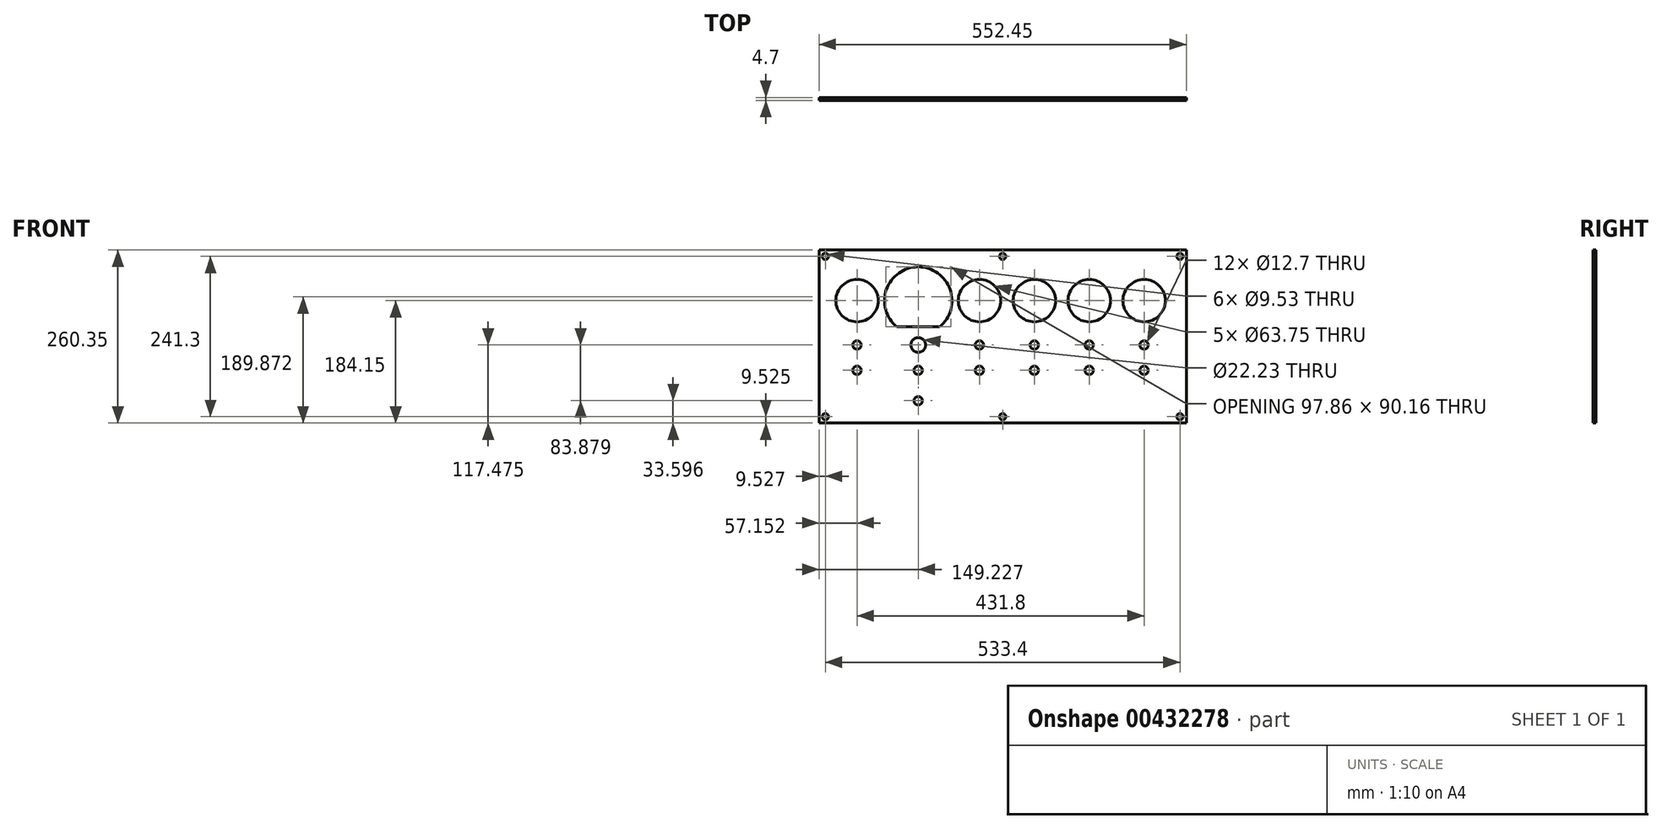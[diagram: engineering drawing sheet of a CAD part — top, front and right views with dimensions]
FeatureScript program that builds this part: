
annotation { "Feature Type Name" : "Feature", "Feature Type Description" : "" }
export const myFeature = defineFeature(function(context is Context, id is Id, definition is map)
    precondition{}
    {
        {
            var Q0;
            Q0=qCreatedBy(makeId("Front.planeOp"),FACE);
            var sketch = newSketch(context, id + "F0", { "sketchPlane" : qUnion([Q0])});
            skPoint(sketch, "E0.middle", {"position": v(0, 0) * mm});
            skLineSegment(sketch, "E1.bottom", {"start": v(-260.34, 165.1) * mm, "end": v(292.11, 165.1) * mm});
            skLineSegment(sketch, "E1.top", {"start": v(-260.34, -95.25) * mm, "end": v(292.11, -95.25) * mm});
            skLineSegment(sketch, "E1.left", {"start": v(-260.34, 165.1) * mm, "end": v(-260.34, -95.25) * mm});
            skLineSegment(sketch, "E1.right", {"start": v(292.11, 165.1) * mm, "end": v(292.11, -95.25) * mm});
            skCircle(sketch, "E2", {"center": v(-203.19, 88.9) * mm, "radius": 31.88 * mm});
            skArc(sketch, "E3", {"start": v(-79, 49.54) * mm, "mid": v(-111.11, 139.7) * mm, "end": v(-143.23, 49.54) * mm});
            skCircle(sketch, "E4", {"center": v(-19.04, 88.9) * mm, "radius": 31.88 * mm});
            skCircle(sketch, "E5", {"center": v(63.51, 88.9) * mm, "radius": 31.88 * mm});
            skCircle(sketch, "E6", {"center": v(146.06, 88.9) * mm, "radius": 31.88 * mm});
            skCircle(sketch, "E7", {"center": v(228.61, 88.9) * mm, "radius": 31.88 * mm});
            skLineSegment(sketch, "E8", {"start": v(-143.23, 49.54) * mm, "end": v(-79, 49.54) * mm});
            skLineSegment(sketch, "E9", {"start": v(-330.98, 34.93) * mm, "end": v(355.64, 34.93) * mm, "construction": true});
            skPoint(sketch, "E9.startSnap0", {"position": v(-260.34, 34.93) * mm});
            skLineSegment(sketch, "E10", {"start": v(15.89, 224.86) * mm, "end": v(15.89, -151.25) * mm, "construction": true});
            skPoint(sketch, "E10.startSnap0", {"position": v(15.89, 165.1) * mm});
            skPoint(sketch, "E11.middle", {"position": v(15.89, 34.93) * mm});
            skCircle(sketch, "E12", {"center": v(282.59, 155.58) * mm, "radius": 4.76 * mm});
            skCircle(sketch, "E13", {"center": v(282.59, -85.72) * mm, "radius": 4.76 * mm});
            skCircle(sketch, "E14", {"center": v(15.89, -85.72) * mm, "radius": 4.76 * mm});
            skCircle(sketch, "E15", {"center": v(-250.81, -85.72) * mm, "radius": 4.76 * mm});
            skCircle(sketch, "E16", {"center": v(-250.81, 155.58) * mm, "radius": 4.76 * mm});
            skCircle(sketch, "E17", {"center": v(15.89, 155.58) * mm, "radius": 4.76 * mm});
            skSolve(sketch);
        }
        {
            var Q0;
            Q0=makeQuery(id+"F0.imprint","IMPRINT",FACE,{"disambiguationData":[TD([[makeQuery(id+"F0.imprint","IMPRINT",EDGE,{"derivedFrom":sQuery(id+"F0.wireOp",EDGE,"E1.bottom")}),-1.0]])]});
            extrude(context, id + "F1", {"entities" : qUnion([Q0]), "oppositeDirection" : true, "depth" : 4.7 * mm, "offsetDistance" : 25.4 * mm});
        }
        {
            var Q0;
            Q0=makeQuery(id+"F1.opExtrude","CAP_FACE",FACE,{"disambiguationData":[OSD([sQuery(id+"F0.wireOp",EDGE,"E0.bottom"),sQuery(id+"F0.wireOp",EDGE,"E0.top"),sQuery(id+"F0.wireOp",EDGE,"E0.left"),sQuery(id+"F0.wireOp",EDGE,"E0.right"),sQuery(id+"F0.wireOp",EDGE,"E1.bottom"),sQuery(id+"F0.wireOp",EDGE,"E2"),sQuery(id+"F0.wireOp",EDGE,"E3"),sQuery(id+"F0.wireOp",EDGE,"E4"),sQuery(id+"F0.wireOp",EDGE,"E5"),sQuery(id+"F0.wireOp",EDGE,"E6"),sQuery(id+"F0.wireOp",EDGE,"E7")])],"isStart":false});
            var sketch = newSketch(context, id + "F2", { "sketchPlane" : qUnion([Q0])});
            skLineSegment(sketch, "E18", {"start": v(203.19, 88.9) * mm, "end": v(203.19, -122.71) * mm, "construction": true});
            skLineSegment(sketch, "E19", {"start": v(19.04, 88.9) * mm, "end": v(19.04, -117.38) * mm, "construction": true});
            skLineSegment(sketch, "E20", {"start": v(-63.51, 88.9) * mm, "end": v(-63.51, -120.63) * mm, "construction": true});
            skLineSegment(sketch, "E21", {"start": v(-146.06, 88.9) * mm, "end": v(-146.06, -122.8) * mm, "construction": true});
            skLineSegment(sketch, "E22", {"start": v(-228.61, 88.9) * mm, "end": v(-228.61, -123.34) * mm, "construction": true});
            skLineSegment(sketch, "E23", {"start": v(260.34, 34.93) * mm, "end": v(260.34, 22.23) * mm, "construction": true});
            skLineSegment(sketch, "E24", {"start": v(260.34, 22.23) * mm, "end": v(316, 22.23) * mm, "construction": true});
            skCircle(sketch, "E25", {"center": v(203.19, 22.23) * mm, "radius": 6.35 * mm});
            skCircle(sketch, "E26", {"center": v(19.04, 22.23) * mm, "radius": 6.35 * mm});
            skCircle(sketch, "E27", {"center": v(-63.51, 22.23) * mm, "radius": 6.35 * mm});
            skCircle(sketch, "E28", {"center": v(-146.06, 22.23) * mm, "radius": 6.35 * mm});
            skCircle(sketch, "E29", {"center": v(-228.61, 22.23) * mm, "radius": 6.35 * mm});
            skLineSegment(sketch, "E30", {"start": v(260.34, 22.23) * mm, "end": v(260.34, -15.87) * mm, "construction": true});
            skLineSegment(sketch, "E31", {"start": v(260.34, -15.87) * mm, "end": v(305.56, -15.87) * mm, "construction": true});
            skCircle(sketch, "E32", {"center": v(203.19, -15.87) * mm, "radius": 6.35 * mm});
            skCircle(sketch, "E33", {"center": v(19.04, -15.87) * mm, "radius": 6.35 * mm});
            skCircle(sketch, "E34", {"center": v(-63.51, -15.87) * mm, "radius": 6.35 * mm});
            skCircle(sketch, "E35", {"center": v(-146.06, -15.87) * mm, "radius": 6.35 * mm});
            skCircle(sketch, "E36", {"center": v(-228.61, -15.87) * mm, "radius": 6.35 * mm});
            skLineSegment(sketch, "E37", {"start": v(111.11, -15.87) * mm, "end": v(203.19, -15.87) * mm, "construction": true});
            skLineSegment(sketch, "E38", {"start": v(111.11, -15.87) * mm, "end": v(111.11, -84.5) * mm, "construction": true});
            skCircle(sketch, "E39", {"center": v(111.11, -15.87) * mm, "radius": 6.35 * mm});
            skCircle(sketch, "E40", {"center": v(111.11, 22.23) * mm, "radius": 11.11 * mm});
            skCircle(sketch, "E41", {"center": v(111.11, -61.65) * mm, "radius": 6.35 * mm});
            skSolve(sketch);
        }
        {
            var Q0;
            Q0=qSketchRegion(id+"F2",true);
            extrude(context, id + "F3", {"entities" : qUnion([Q0]), "operationType" : NewBodyOperationType.REMOVE, "oppositeDirection" : true, "depth" : 25.4 * mm});
        }
        {
            var Q0;
            Q0=makeQuery(id+"F1.opExtrude","CAP_FACE",FACE,{"disambiguationData":[OSD([sQuery(id+"F0.wireOp",EDGE,"E0.bottom"),sQuery(id+"F0.wireOp",EDGE,"E0.top"),sQuery(id+"F0.wireOp",EDGE,"E0.left"),sQuery(id+"F0.wireOp",EDGE,"E0.right"),sQuery(id+"F0.wireOp",EDGE,"E1.bottom"),sQuery(id+"F0.wireOp",EDGE,"E2"),sQuery(id+"F0.wireOp",EDGE,"E3"),sQuery(id+"F0.wireOp",EDGE,"E4"),sQuery(id+"F0.wireOp",EDGE,"E5"),sQuery(id+"F0.wireOp",EDGE,"E6"),sQuery(id+"F0.wireOp",EDGE,"E7")])],"isStart":false});
            var sketch = newSketch(context, id + "F4", { "sketchPlane" : qUnion([Q0])});
            skPoint(sketch, "E42.middle", {"position": v(111.11, 88.9) * mm});
            skCircle(sketch, "E43", {"center": v(79.36, 120.65) * mm, "radius": 2.41 * mm});
            skCircle(sketch, "E44", {"center": v(142.86, 120.65) * mm, "radius": 2.41 * mm});
            skCircle(sketch, "E45", {"center": v(142.86, 57.15) * mm, "radius": 2.41 * mm});
            skCircle(sketch, "E46", {"center": v(79.36, 57.15) * mm, "radius": 2.41 * mm});
            skSolve(sketch);
        }
        {
            var Q0;
            Q0=qSketchRegion(id+"F4",true);
            extrude(context, id + "F5", {"entities" : qUnion([Q0]), "operationType" : NewBodyOperationType.REMOVE, "oppositeDirection" : true, "depth" : 25.4 * mm});
        }
    });
